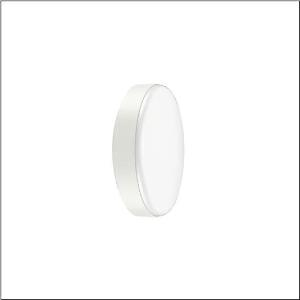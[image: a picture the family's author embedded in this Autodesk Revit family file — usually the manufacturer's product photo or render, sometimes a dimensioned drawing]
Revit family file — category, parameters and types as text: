
# Revit family: rondel_31_51wc10da42as
name_source: partatom
category: Lighting Fixtures
units: mm (PartAtom-declared; Revit-internal decimal feet)

## family parameters
Cut with Voids When Loaded = No
Host = Face
Light Source = No
Part Type = Normal
Room Calculation Point = No
Round Connector Dimension = Use Diameter
Shared = No

## types (1)
- Rondel 31 (1 x LED, 2550 lm, 20.5 W, 4000K)
    Apparent Load = 21 VA
    CIE Flux Codes = 44 75 94 94 100
    Color Rendering = 80
    Color Temperature = 4000K
    Default Elevation = 1800 mm
    Description = Rondel 31, wall and ceiling luminaire, primary optical cover: cover, of PC, opal, light emission: direct distribution, primary light characteristic: symmetric, installation type: surface-mounted, LED, rated luminous flux: 2.550lm, luminous efficacy: 124lm/W, light colour: 840, colour temperature: 4000K, with terminal, 5-pole, max. 2.5mm², mains connection: 220..240V, AC, 50/60Hz, rated input power: 20.5W, luminaire housing, of PC, traffic white (RAL 9016), diameter: 350mm, brightness and presence sensor, HF sensor, protection rating (complete): IP65, insulation class (complete): insulation class II (safety insulation), certification: CE, impact resistance: IK10, permissible operating ambient temperature: -20..+40°C, permissible storage temperature: -20..+60°C, packaging unit: 1 piece
    Height = 97 mm
    Lamp = 1 x LED
    Lamp Light Flux = 2550 lm
    Lamp Power = 20.5 W
    Lamp count = 1
    Length = 350 mm
    Luminous efficacy = 124 lm/W
    Manufacturer = Siteco
    ModVariant = No
    Model = 51WC10DA42AS
    Mounting Place = Ceiling
    Mounting Type = Surface mounted
    Number of Poles = 1
    OnlyDefault = Yes
    Power Factor = 1
    Product Name = Rondel 31
    Product group = wall and ceiling luminaire
    ProductGroupID = 302
    Protection Class = Protection class II
    Protection Degree = IP 65
    RLX_Detail_Level = 1
    RLX_Emergency_Light_Flux = 0 lm
    RLX_Emergency_Type = 0
    RLX_Emergency_Type_DB = No
    RlxData = <blob elided: 29777 chars, md5=0a8a9221>
    Socket = socket
    Standby Power = 0 W
    System Light Flux = 2550 lm
    System Power = 21 W
    Type Comments = Product without accessories
    Type Image = l_1007027.jpg
    URL = http://relux.com
    VarID = ---
    Voltage = 0 V
    Weight = 0.00 kg
    Width = 0 mm  [stored 0 ft]

note: [stored X ft] marks values corroborated as IEEE doubles in the binary element streams (Revit-internal decimal feet)

## geometry (parser evidence)
native form markers: Blend x4, Sweep x12
no freeform markers — native parametric forms only
